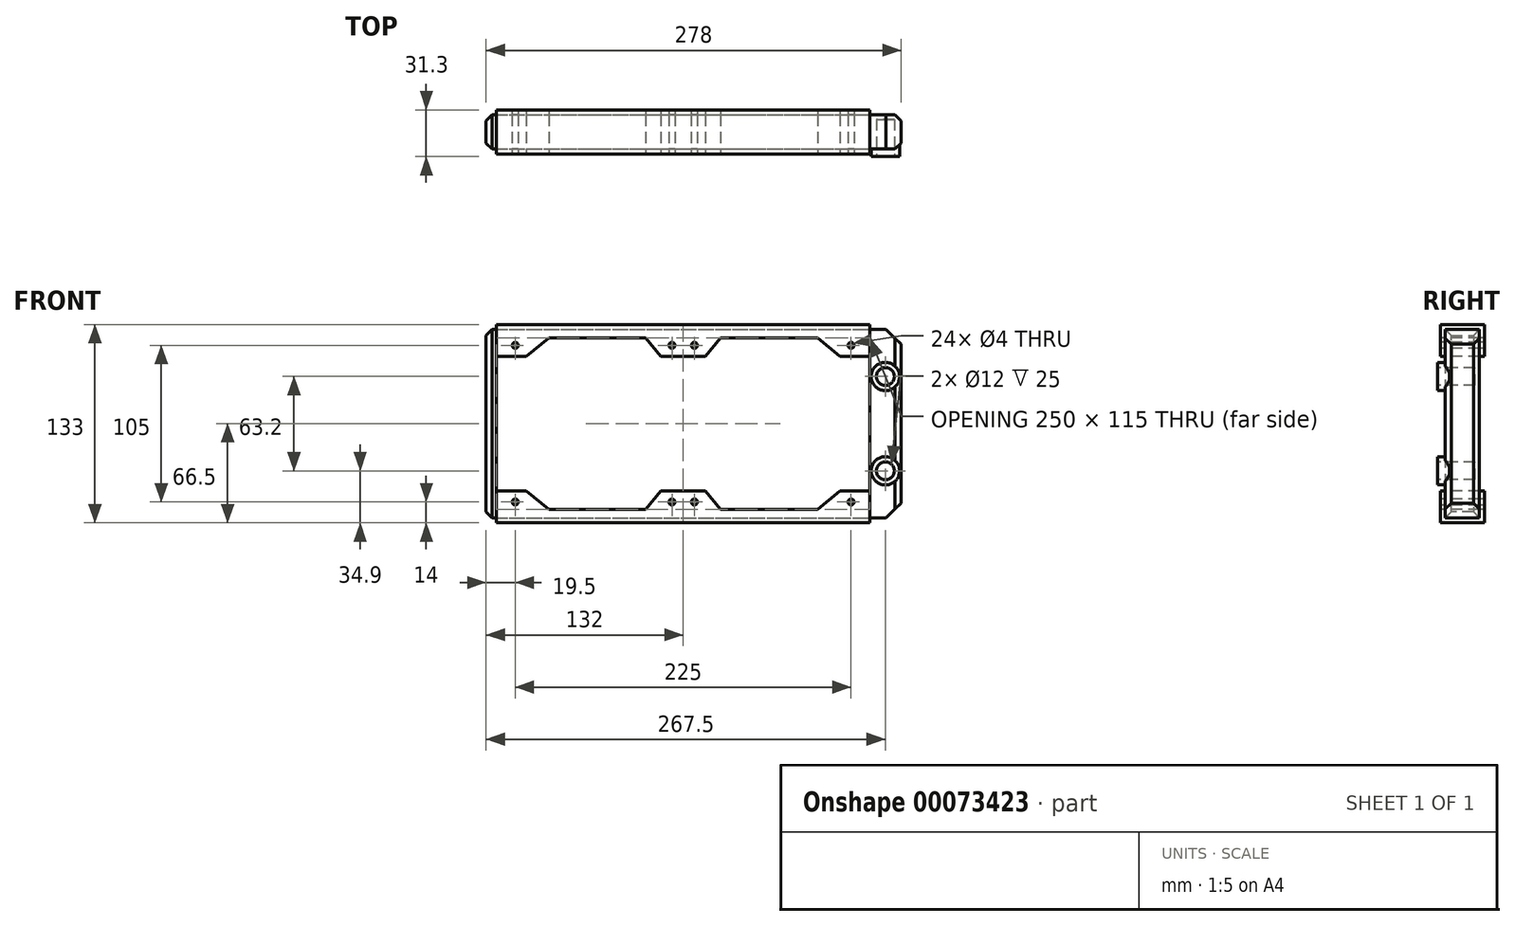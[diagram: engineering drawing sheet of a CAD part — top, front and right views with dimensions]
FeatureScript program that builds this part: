
annotation { "Feature Type Name" : "Feature", "Feature Type Description" : "" }
export const myFeature = defineFeature(function(context is Context, id is Id, definition is map)
    precondition{}
    {
        {
            var Q0;
            Q0=qCreatedBy(makeId("Front.planeOp"),FACE);
            var sketch = newSketch(context, id + "F0", { "sketchPlane" : qUnion([Q0])});
            skLineSegment(sketch, "E0.bottom", {"start": v(0, 63.2) * mm, "end": v(278, 63.2) * mm});
            skLineSegment(sketch, "E0.top", {"start": v(0, -63.2) * mm, "end": v(278, -63.2) * mm});
            skLineSegment(sketch, "E0.left", {"start": v(0, 63.2) * mm, "end": v(0, -63.2) * mm});
            skLineSegment(sketch, "E0.right", {"start": v(278, 63.2) * mm, "end": v(278, -63.2) * mm});
            skPoint(sketch, "E1", {"position": v(0, 0) * mm});
            skSolve(sketch);
        }
        {
            var Q0;
            Q0=qSketchRegion(id+"F0",true);
            extrude(context, id + "F1", {"entities" : qUnion([Q0]), "depth" : 23 * mm});
        }
        {
            var Q0;
            Q0=makeQuery(id+"F1.opExtrude","CAP_FACE",FACE,{"disambiguationData":[OSD([sQuery(id+"F0.wireOp",EDGE,"E0.bottom"),sQuery(id+"F0.wireOp",EDGE,"E0.top"),sQuery(id+"F0.wireOp",EDGE,"E0.left"),sQuery(id+"F0.wireOp",EDGE,"E0.right")])],"isStart":false});
            var sketch = newSketch(context, id + "F2", { "sketchPlane" : qUnion([Q0])});
            skCircle(sketch, "E2", {"center": v(267.5, 31.6) * mm, "radius": 9.5 * mm});
            skCircle(sketch, "E3", {"center": v(267.5, -31.6) * mm, "radius": 9.5 * mm});
            skLineSegment(sketch, "E4", {"start": v(278, 0) * mm, "end": v(0, 0) * mm, "construction": true});
            skSolve(sketch);
        }
        {
            var Q0;
            Q0=qSketchRegion(id+"F2",true);
            extrude(context, id + "F3", {"entities" : qUnion([Q0]), "operationType" : NewBodyOperationType.ADD, "depth" : 5 * mm});
        }
        {
            var Q0;
            Q0=makeQuery(id+"F3.opExtrude","CAP_FACE",FACE,{"disambiguationData":[OSD([sQuery(id+"F2.wireOp",EDGE,"E2")])],"isStart":false});
            var sketch = newSketch(context, id + "F4", { "sketchPlane" : qUnion([Q0])});
            skCircle(sketch, "E5", {"center": v(267.5, 31.6) * mm, "radius": 6 * mm});
            skCircle(sketch, "E6", {"center": v(267.5, -31.6) * mm, "radius": 6 * mm});
            skSolve(sketch);
        }
        {
            var Q0;
            Q0=qSketchRegion(id+"F4",true);
            extrude(context, id + "F5", {"entities" : qUnion([Q0]), "operationType" : NewBodyOperationType.REMOVE, "oppositeDirection" : true, "depth" : 25 * mm});
        }
        {
            var Q0;
            Q0=makeQuery(id+"F1.opExtrude","SWEPT_EDGE",EDGE,{"disambiguationData":[OSD([sQuery(id+"F0.wireOp",EDGE,"E0.top"),sQuery(id+"F0.wireOp",EDGE,"E0.right")])]});
            var Q1;
            Q1=makeQuery(id+"F1.opExtrude","SWEPT_EDGE",EDGE,{"disambiguationData":[OSD([sQuery(id+"F0.wireOp",EDGE,"E0.bottom"),sQuery(id+"F0.wireOp",EDGE,"E0.right")])]});
            chamfer(context, id + "F6", {"entities" : qUnion([Q0, Q1]), "width" : 10 * mm, "tangentPropagation" : true});
        }
        {
            var Q0;
            Q0=makeQuery(id+"F1.opExtrude","CAP_EDGE",EDGE,{"disambiguationData":[OSD([sQuery(id+"F0.wireOp",EDGE,"E0.right")])],"isStart":false});
            var Q1;
            Q1=makeQuery(id+"F1.opExtrude","CAP_EDGE",EDGE,{"disambiguationData":[OSD([sQuery(id+"F0.wireOp",EDGE,"E0.right")])],"isStart":true});
            var Q2;
            Q2=makeQuery(id+"F1.opExtrude","CAP_EDGE",EDGE,{"disambiguationData":[OSD([sQuery(id+"F0.wireOp",EDGE,"E0.left")])],"isStart":false});
            var Q3;
            Q3=makeQuery(id+"F1.opExtrude","CAP_EDGE",EDGE,{"disambiguationData":[OSD([sQuery(id+"F0.wireOp",EDGE,"E0.left")])],"isStart":true});
            var Q4;
            Q4=makeQuery(id+"F1.opExtrude","SWEPT_EDGE",EDGE,{"disambiguationData":[OSD([sQuery(id+"F0.wireOp",EDGE,"E0.top"),sQuery(id+"F0.wireOp",EDGE,"E0.left")])]});
            var Q5;
            Q5=makeQuery(id+"F1.opExtrude","SWEPT_EDGE",EDGE,{"disambiguationData":[OSD([sQuery(id+"F0.wireOp",EDGE,"E0.bottom"),sQuery(id+"F0.wireOp",EDGE,"E0.left")])]});
            chamfer(context, id + "F7", {"entities" : qUnion([Q0, Q1, Q2, Q3, Q4, Q5]), "width" : 4 * mm, "tangentPropagation" : true});
        }
        {
            var Q0;
            Q0=makeQuery(id+"F1.opExtrude","SWEPT_FACE",FACE,{"disambiguationData":[OSD([sQuery(id+"F0.wireOp",EDGE,"E0.left")])]});
            cPlane(context, id + "F8", {"entities" : qUnion([Q0]), "cplaneType" : CPlaneType.OFFSET, "offset" : 7 * mm, "oppositeDirection" : true, "width" : 150 * mm, "height" : 150 * mm});
        }
        {
            var Q0;
            Q0=qCreatedBy(id+"F8.planeOp",FACE);
            var sketch = newSketch(context, id + "F9", { "sketchPlane" : qUnion([Q0])});
            skLineSegment(sketch, "E7.bottom", {"start": v(-3.3, 66.5) * mm, "end": v(26.3, 66.5) * mm});
            skLineSegment(sketch, "E7.top", {"start": v(-3.3, -66.5) * mm, "end": v(26.3, -66.5) * mm});
            skLineSegment(sketch, "E7.left", {"start": v(-3.3, 66.5) * mm, "end": v(-3.3, -66.5) * mm});
            skLineSegment(sketch, "E7.right", {"start": v(26.3, 66.5) * mm, "end": v(26.3, -66.5) * mm});
            skLineSegment(sketch, "E8", {"start": v(0, 0) * mm, "end": v(-3.3, 0) * mm, "construction": true});
            skLineSegment(sketch, "E9.bottom", {"start": v(0, 63.2) * mm, "end": v(23, 63.2) * mm});
            skLineSegment(sketch, "E9.top", {"start": v(0, -63.2) * mm, "end": v(23, -63.2) * mm});
            skLineSegment(sketch, "E9.left", {"start": v(0, 63.2) * mm, "end": v(0, -63.2) * mm});
            skLineSegment(sketch, "E9.right", {"start": v(23, 63.2) * mm, "end": v(23, -63.2) * mm});
            skSolve(sketch);
        }
        {
            var Q0;
            Q0=qSketchRegion(id+"F9",true);
            extrude(context, id + "F10", {"entities" : qUnion([Q0]), "oppositeDirection" : true, "depth" : 250 * mm});
        }
        {
            var Q0;
            Q0=makeQuery(id+"F10.opExtrude","SWEPT_FACE",FACE,{"disambiguationData":[OSD([sQuery(id+"F9.wireOp",EDGE,"E7.right")])]});
            var sketch = newSketch(context, id + "F11", { "sketchPlane" : qUnion([Q0])});
            skCircle(sketch, "E10", {"center": v(19.5, 52.5) * mm, "radius": 2 * mm});
            skCircle(sketch, "E11", {"center": v(124.5, 52.5) * mm, "radius": 2 * mm});
            skCircle(sketch, "E12", {"center": v(139.5, 52.5) * mm, "radius": 2 * mm});
            skCircle(sketch, "E13", {"center": v(244.5, 52.5) * mm, "radius": 2 * mm});
            skLineSegment(sketch, "E14", {"start": v(7, 0) * mm, "end": v(257, 0) * mm, "construction": true});
            skLineSegment(sketch, "E15", {"start": v(132, 66.5) * mm, "end": v(132, -66.5) * mm, "construction": true});
            skCircle(sketch, "E16.MirrorC", {"center": v(19.5, -52.5) * mm, "radius": 2 * mm});
            skCircle(sketch, "E17.MirrorC", {"center": v(124.5, -52.5) * mm, "radius": 2 * mm});
            skCircle(sketch, "E18.MirrorC", {"center": v(139.5, -52.5) * mm, "radius": 2 * mm});
            skCircle(sketch, "E19.MirrorC", {"center": v(244.5, -52.5) * mm, "radius": 2 * mm});
            skSolve(sketch);
        }
        {
            var Q0;
            Q0=qSketchRegion(id+"F11",true);
            extrude(context, id + "F12", {"entities" : qUnion([Q0]), "operationType" : NewBodyOperationType.REMOVE, "endBound" : BoundingType.THROUGH_ALL, "oppositeDirection" : true, "depth" : 25 * mm});
        }
        {
            var Q0;
            Q0=makeQuery(id+"F10.opExtrude","SWEPT_FACE",FACE,{"disambiguationData":[OSD([sQuery(id+"F9.wireOp",EDGE,"E7.right")])]});
            var sketch = newSketch(context, id + "F13", { "sketchPlane" : qUnion([Q0])});
            skLineSegment(sketch, "E20", {"start": v(7, 45) * mm, "end": v(27, 45) * mm});
            skLineSegment(sketch, "E21", {"start": v(27, 45) * mm, "end": v(42, 57.5) * mm});
            skLineSegment(sketch, "E22", {"start": v(42, 57.5) * mm, "end": v(107, 57.5) * mm});
            skLineSegment(sketch, "E23", {"start": v(107, 57.5) * mm, "end": v(117, 45) * mm});
            skLineSegment(sketch, "E24", {"start": v(117, 45) * mm, "end": v(147, 45) * mm});
            skLineSegment(sketch, "E25", {"start": v(147, 45) * mm, "end": v(157, 57.5) * mm});
            skLineSegment(sketch, "E26", {"start": v(157, 57.5) * mm, "end": v(222, 57.5) * mm});
            skLineSegment(sketch, "E27", {"start": v(222, 57.5) * mm, "end": v(237, 45) * mm});
            skLineSegment(sketch, "E28", {"start": v(237, 45) * mm, "end": v(257, 45) * mm});
            skLineSegment(sketch, "E29", {"start": v(257, 45) * mm, "end": v(257, 0) * mm});
            skLineSegment(sketch, "E30", {"start": v(7, 45) * mm, "end": v(7, 0) * mm});
            skLineSegment(sketch, "E31", {"start": v(7, 0) * mm, "end": v(257, 0) * mm, "construction": true});
            skLineSegment(sketch, "E32", {"start": v(132, 66.5) * mm, "end": v(132, 45) * mm, "construction": true});
            skLineSegment(sketch, "E33.MirrorCS", {"start": v(257, -45) * mm, "end": v(257, 0) * mm});
            skLineSegment(sketch, "E34.MirrorCS", {"start": v(237, -45) * mm, "end": v(257, -45) * mm});
            skLineSegment(sketch, "E35.MirrorCS", {"start": v(222, -57.5) * mm, "end": v(237, -45) * mm});
            skLineSegment(sketch, "E36.MirrorCS", {"start": v(157, -57.5) * mm, "end": v(222, -57.5) * mm});
            skLineSegment(sketch, "E37.MirrorCS", {"start": v(147, -45) * mm, "end": v(157, -57.5) * mm});
            skLineSegment(sketch, "E38.MirrorCS", {"start": v(117, -45) * mm, "end": v(147, -45) * mm});
            skLineSegment(sketch, "E39.MirrorCS", {"start": v(107, -57.5) * mm, "end": v(117, -45) * mm});
            skLineSegment(sketch, "E40.MirrorCS", {"start": v(42, -57.5) * mm, "end": v(107, -57.5) * mm});
            skLineSegment(sketch, "E41.MirrorCS", {"start": v(27, -45) * mm, "end": v(42, -57.5) * mm});
            skLineSegment(sketch, "E42.MirrorCS", {"start": v(7, -45) * mm, "end": v(7, 0) * mm});
            skLineSegment(sketch, "E43.MirrorCS", {"start": v(7, -45) * mm, "end": v(27, -45) * mm});
            skSolve(sketch);
        }
        {
            var Q0;
            Q0=qSketchRegion(id+"F13",true);
            extrude(context, id + "F14", {"entities" : qUnion([Q0]), "operationType" : NewBodyOperationType.REMOVE, "endBound" : BoundingType.THROUGH_ALL, "oppositeDirection" : true, "depth" : 25 * mm});
        }
    });
